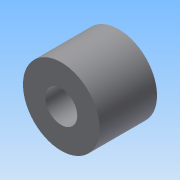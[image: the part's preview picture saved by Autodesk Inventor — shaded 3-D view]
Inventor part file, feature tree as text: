
AUTODESK INVENTOR PART (.ipt)
format: ipt  version: 2015 (Build 190159000, 159)  size: 79,872 bytes
history: native  units: mm
features: extrude x1, sketch x1
ambient origin geometry x8: Origin, YZ Plane, XZ Plane, XY Plane, X Axis, Y Axis, Z Axis, Center Point
bodies: Solid1 (feature_tree)
feature tree (2):
  extrude  "Extrusion1"  Depth=9.0mm
  sketch  "Sketch1"  dims[d0=12.0mm d1=5.0mm d2=9.0mm d3=0.0mm]
